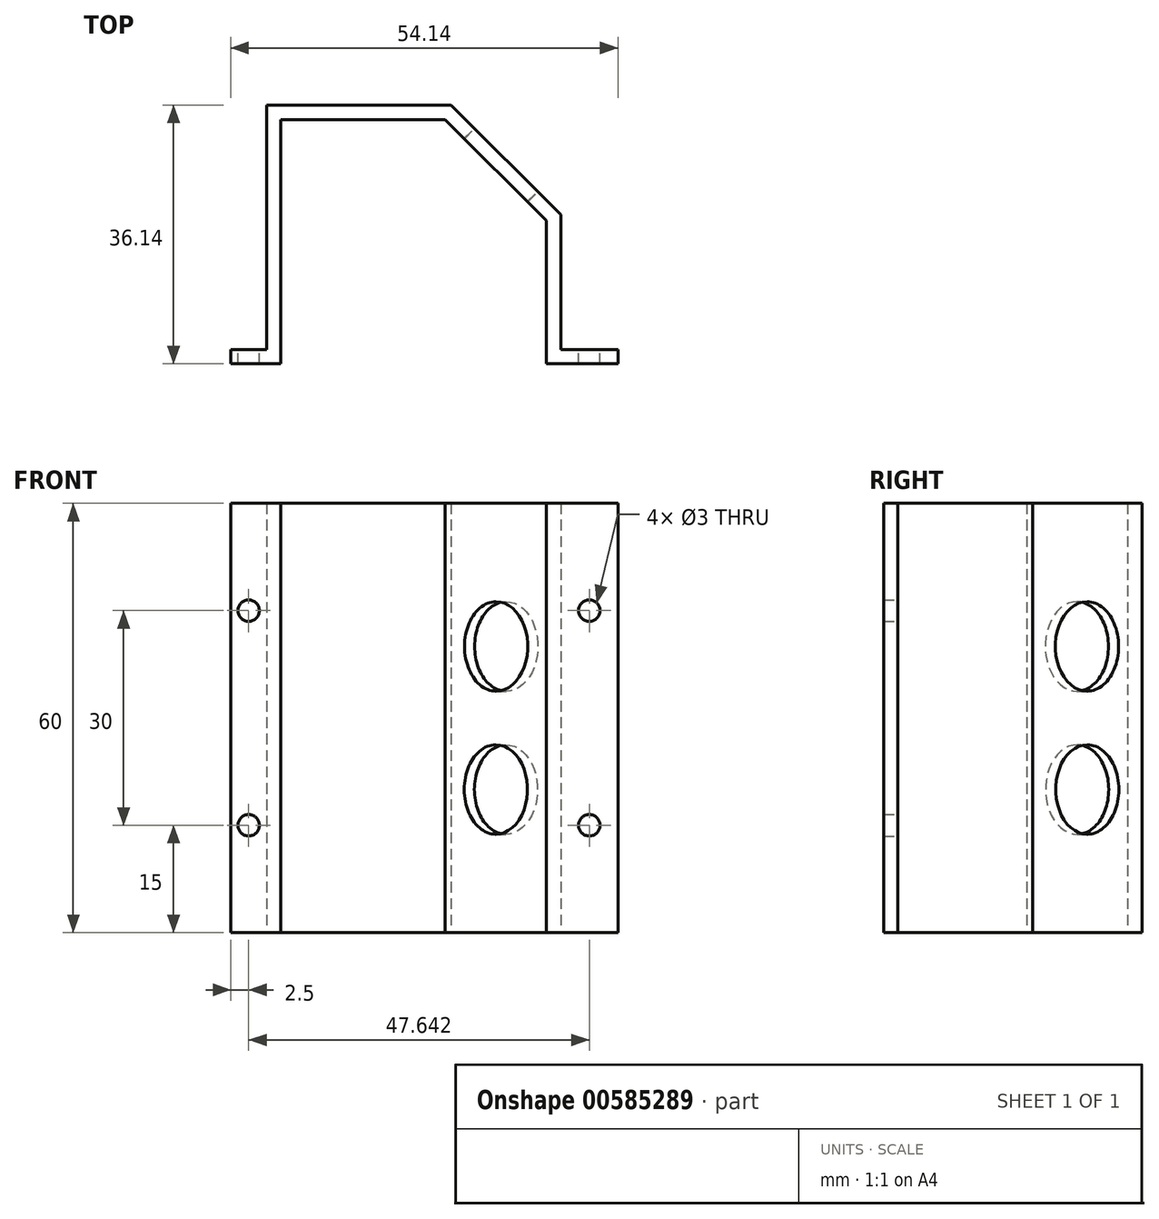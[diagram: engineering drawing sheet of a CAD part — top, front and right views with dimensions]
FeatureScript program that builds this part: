
annotation { "Feature Type Name" : "Feature", "Feature Type Description" : "" }
export const myFeature = defineFeature(function(context is Context, id is Id, definition is map)
    precondition{}
    {
        {
            var Q0;
            Q0=qCreatedBy(makeId("Top.planeOp"),FACE);
            var sketch = newSketch(context, id + "F0", { "sketchPlane" : qUnion([Q0])});
            skLineSegment(sketch, "E0", {"start": v(0, 0) * mm, "end": v(7, 0) * mm});
            skLineSegment(sketch, "E1", {"start": v(7, 0) * mm, "end": v(7, 34.14) * mm});
            skLineSegment(sketch, "E2", {"start": v(7, 34.14) * mm, "end": v(30, 34.14) * mm});
            skLineSegment(sketch, "E3", {"start": v(30, 34.14) * mm, "end": v(44.14, 20) * mm});
            skLineSegment(sketch, "E4", {"start": v(44.14, 20) * mm, "end": v(44.14, 0) * mm});
            skLineSegment(sketch, "E5", {"start": v(44.14, 0) * mm, "end": v(54.14, 0) * mm});
            skLineSegment(sketch, "E6.0", {"start": v(46.14, 2) * mm, "end": v(54.14, 2) * mm});
            skLineSegment(sketch, "E6.1", {"start": v(46.14, 20.83) * mm, "end": v(46.14, 2) * mm});
            skLineSegment(sketch, "E6.2", {"start": v(0, 2) * mm, "end": v(5, 2) * mm});
            skLineSegment(sketch, "E6.3", {"start": v(5, 2) * mm, "end": v(5, 36.14) * mm});
            skLineSegment(sketch, "E6.4", {"start": v(5, 36.14) * mm, "end": v(30.83, 36.14) * mm});
            skLineSegment(sketch, "E6.5", {"start": v(30.83, 36.14) * mm, "end": v(46.14, 20.83) * mm});
            skLineSegment(sketch, "E7", {"start": v(54.14, 0) * mm, "end": v(54.14, 2) * mm});
            skLineSegment(sketch, "E8", {"start": v(0, 0) * mm, "end": v(0, 2) * mm});
            skSolve(sketch);
        }
        {
            var Q0;
            Q0=makeQuery(id+"F0.imprint","IMPRINT",FACE,{"disambiguationData":[TD([[makeQuery(id+"F0.imprint","IMPRINT",EDGE,{"derivedFrom":sQuery(id+"F0.wireOp",EDGE,"E0")}),1.0]])]});
            extrude(context, id + "F1", {"entities" : qUnion([Q0]), "depth" : 60 * mm, "offsetDistance" : 25 * mm});
        }
        {
            var Q0;
            Q0=makeQuery(id+"F1.opExtrude","SWEPT_FACE",FACE,{"disambiguationData":[OSD([sQuery(id+"F0.wireOp",EDGE,"E6.5")])]});
            var sketch = newSketch(context, id + "F2", { "sketchPlane" : qUnion([Q0])});
            skCircle(sketch, "E9", {"center": v(-7.13, 40) * mm, "radius": 6.25 * mm});
            skCircle(sketch, "E10", {"center": v(-7.07, 20) * mm, "radius": 6.25 * mm});
            skPoint(sketch, "E11.orphan", {"position": v(-7.07, 60) * mm});
            skPoint(sketch, "E12.end.orphan", {"position": v(-7.07, 0) * mm});
            skPoint(sketch, "E13.orphan", {"position": v(-12.43, 20) * mm});
            skPoint(sketch, "E14.orphan", {"position": v(-1.83, 40) * mm});
            skPoint(sketch, "E15.start.orphan", {"position": v(-12.43, 40) * mm});
            skSolve(sketch);
        }
        {
            var Q0;
            Q0=makeQuery(id+"F2.imprint","IMPRINT",FACE,{"disambiguationData":[TD([[makeQuery(id+"F2.imprint","IMPRINT",EDGE,{"derivedFrom":sQuery(id+"F2.wireOp",EDGE,"E9")}),1.0]])]});
            extrude(context, id + "F3", {"entities" : qUnion([Q0]), "operationType" : NewBodyOperationType.REMOVE, "oppositeDirection" : true, "depth" : 2 * mm, "offsetDistance" : 25 * mm});
        }
        {
            var Q0;
            Q0=makeQuery(id+"F2.imprint","IMPRINT",FACE,{"disambiguationData":[TD([[makeQuery(id+"F2.imprint","IMPRINT",EDGE,{"derivedFrom":sQuery(id+"F2.wireOp",EDGE,"E10")}),1.0]])]});
            extrude(context, id + "F4", {"entities" : qUnion([Q0]), "operationType" : NewBodyOperationType.REMOVE, "oppositeDirection" : true, "depth" : 2 * mm, "offsetDistance" : 25 * mm});
        }
        {
            var Q0;
            Q0=makeQuery(id+"F1.opExtrude","SWEPT_FACE",FACE,{"disambiguationData":[OSD([sQuery(id+"F0.wireOp",EDGE,"E6.0")])]});
            var sketch = newSketch(context, id + "F5", { "sketchPlane" : qUnion([Q0])});
            skCircle(sketch, "E16", {"center": v(-50.14, 45) * mm, "radius": 1.5 * mm});
            skCircle(sketch, "E17", {"center": v(-50.14, 15) * mm, "radius": 1.5 * mm});
            skPoint(sketch, "E18.orphan", {"position": v(-46.14, 60) * mm});
            skPoint(sketch, "E19.orphan", {"position": v(-50.14, 60) * mm});
            skPoint(sketch, "E20.end.orphan", {"position": v(-54.14, 30) * mm});
            skPoint(sketch, "E20.start.orphan", {"position": v(-50.14, 30) * mm});
            skPoint(sketch, "E21.orphan", {"position": v(-46.14, 0) * mm});
            skPoint(sketch, "E22.orphan", {"position": v(-50.14, 0) * mm});
            skSolve(sketch);
        }
        {
            var Q0;
            Q0=makeQuery(id+"F5.imprint","IMPRINT",FACE,{"disambiguationData":[TD([[makeQuery(id+"F5.imprint","IMPRINT",EDGE,{"derivedFrom":sQuery(id+"F5.wireOp",EDGE,"E16")}),1.0]])]});
            var Q1;
            Q1=makeQuery(id+"F5.imprint","IMPRINT",FACE,{"disambiguationData":[TD([[makeQuery(id+"F5.imprint","IMPRINT",EDGE,{"derivedFrom":sQuery(id+"F5.wireOp",EDGE,"E17")}),1.0]])]});
            extrude(context, id + "F6", {"entities" : qUnion([Q0, Q1]), "operationType" : NewBodyOperationType.REMOVE, "oppositeDirection" : true, "depth" : 2 * mm, "offsetDistance" : 25 * mm});
        }
        {
            var Q0;
            Q0=makeQuery(id+"F1.opExtrude","SWEPT_FACE",FACE,{"disambiguationData":[OSD([sQuery(id+"F0.wireOp",EDGE,"E6.2")])]});
            var sketch = newSketch(context, id + "F7", { "sketchPlane" : qUnion([Q0])});
            skCircle(sketch, "E23", {"center": v(-2.5, 45) * mm, "radius": 1.5 * mm});
            skCircle(sketch, "E24", {"center": v(-2.5, 15) * mm, "radius": 1.5 * mm});
            skPoint(sketch, "E25.orphan", {"position": v(-2.5, 0) * mm});
            skPoint(sketch, "E26.orphan", {"position": v(-5, 0) * mm});
            skPoint(sketch, "E27.end.orphan", {"position": v(0, 30) * mm});
            skPoint(sketch, "E27.start.orphan", {"position": v(-2.5, 30) * mm});
            skPoint(sketch, "E28.orphan", {"position": v(-5, 60) * mm});
            skPoint(sketch, "E29.orphan", {"position": v(-2.5, 60) * mm});
            skSolve(sketch);
        }
        {
            var Q0;
            Q0=makeQuery(id+"F7.imprint","IMPRINT",FACE,{"disambiguationData":[TD([[makeQuery(id+"F7.imprint","IMPRINT",EDGE,{"derivedFrom":sQuery(id+"F7.wireOp",EDGE,"E24")}),1.0]])]});
            var Q1;
            Q1=makeQuery(id+"F7.imprint","IMPRINT",FACE,{"disambiguationData":[TD([[makeQuery(id+"F7.imprint","IMPRINT",EDGE,{"derivedFrom":sQuery(id+"F7.wireOp",EDGE,"E23")}),1.0]])]});
            extrude(context, id + "F8", {"entities" : qUnion([Q0, Q1]), "operationType" : NewBodyOperationType.REMOVE, "oppositeDirection" : true, "depth" : 2 * mm, "offsetDistance" : 25 * mm});
        }
    });
